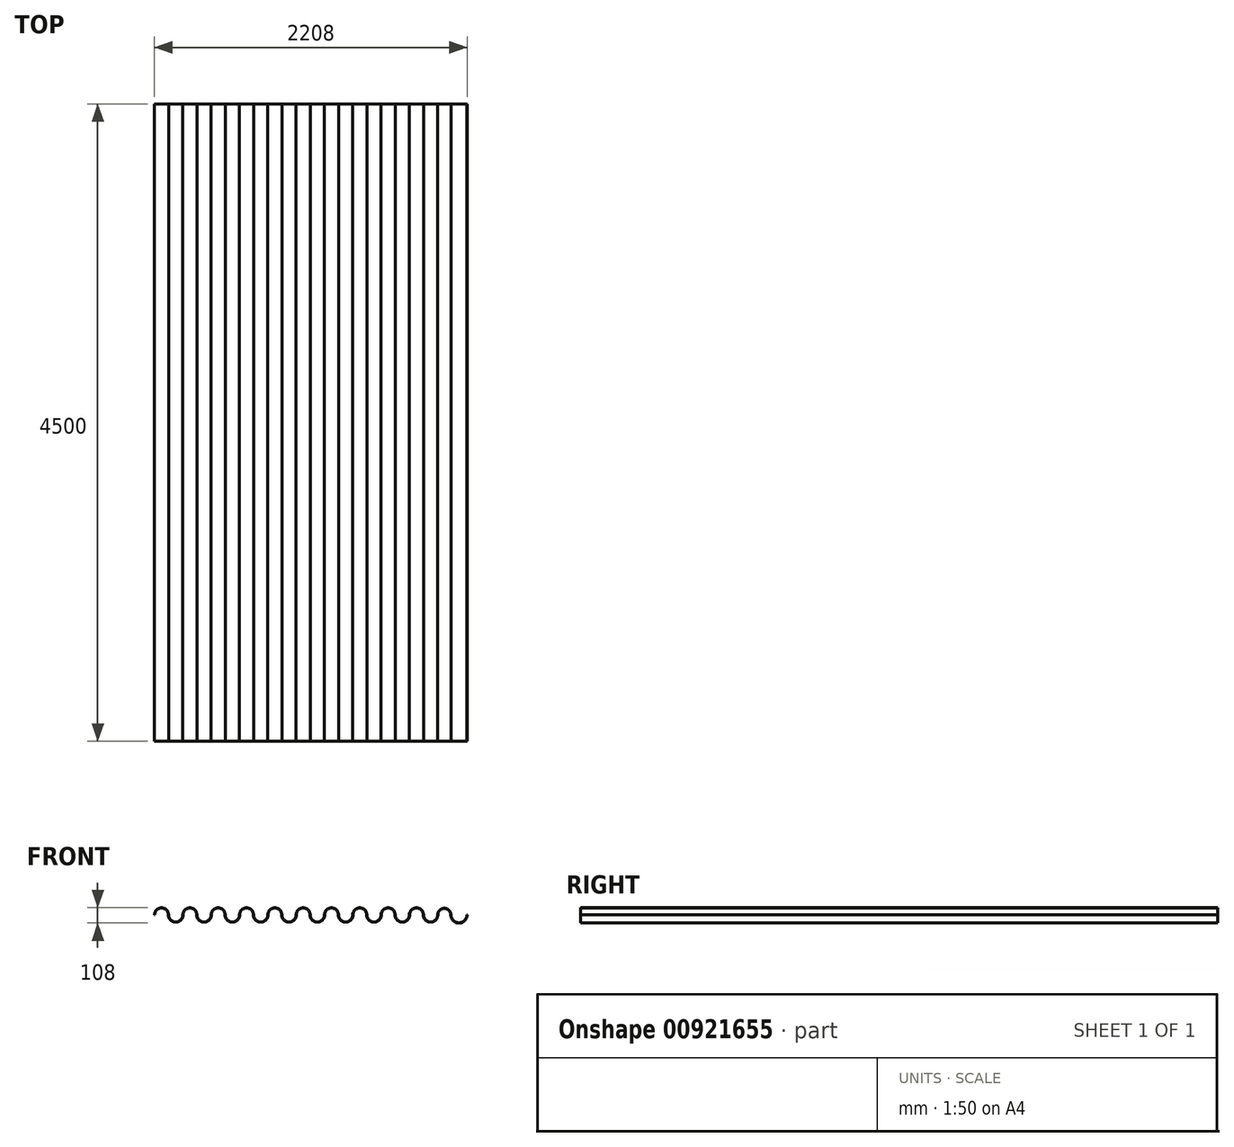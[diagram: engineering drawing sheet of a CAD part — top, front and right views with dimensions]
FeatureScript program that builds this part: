
annotation { "Feature Type Name" : "Feature", "Feature Type Description" : "" }
export const myFeature = defineFeature(function(context is Context, id is Id, definition is map)
    precondition{}
    {
        {
            var Q0;
            Q0=qCreatedBy(makeId("Front.planeOp"),FACE);
            var sketch = newSketch(context, id + "F0", { "sketchPlane" : qUnion([Q0])});
            skArc(sketch, "E0", {"start": v(50, 0) * mm, "mid": v(0, 50) * mm, "end": v(-50, 0) * mm});
            skArc(sketch, "E1", {"start": v(50, 0) * mm, "mid": v(100, -50) * mm, "end": v(150, 0) * mm});
            skArc(sketch, "E2", {"start": v(150, 0) * mm, "mid": v(200, 50) * mm, "end": v(250, 0) * mm});
            skArc(sketch, "E3", {"start": v(250, 0) * mm, "mid": v(300, -50) * mm, "end": v(350, 0) * mm});
            skArc(sketch, "E4", {"start": v(350, 0) * mm, "mid": v(400, 50) * mm, "end": v(450, 0) * mm});
            skArc(sketch, "E5", {"start": v(450, 0) * mm, "mid": v(500, -50) * mm, "end": v(550, 0) * mm});
            skArc(sketch, "E6", {"start": v(550, 0) * mm, "mid": v(600, 50) * mm, "end": v(650, 0) * mm});
            skArc(sketch, "E7", {"start": v(650, 0) * mm, "mid": v(700, -50) * mm, "end": v(750, 0) * mm});
            skArc(sketch, "E8", {"start": v(750, 0) * mm, "mid": v(800, 50) * mm, "end": v(850, 0) * mm});
            skArc(sketch, "E9", {"start": v(850, 0) * mm, "mid": v(900, -50) * mm, "end": v(950, 0) * mm});
            skArc(sketch, "E10", {"start": v(950, 0) * mm, "mid": v(1000, 50) * mm, "end": v(1050, 0) * mm});
            skArc(sketch, "E11", {"start": v(1050, 0) * mm, "mid": v(1100, -50) * mm, "end": v(1150, 0) * mm});
            skArc(sketch, "E12", {"start": v(1150, 0) * mm, "mid": v(1200, 50) * mm, "end": v(1250, 0) * mm});
            skArc(sketch, "E13", {"start": v(1250, 0) * mm, "mid": v(1300, -50) * mm, "end": v(1350, 0) * mm});
            skArc(sketch, "E14", {"start": v(1350, 0) * mm, "mid": v(1400, 50) * mm, "end": v(1450, 0) * mm});
            skArc(sketch, "E15", {"start": v(1450, 0) * mm, "mid": v(1500, -50) * mm, "end": v(1550, 0) * mm});
            skArc(sketch, "E16", {"start": v(1550, 0) * mm, "mid": v(1600, 50) * mm, "end": v(1650, 0) * mm});
            skArc(sketch, "E17", {"start": v(1650, 0) * mm, "mid": v(1700, -50) * mm, "end": v(1750, 0) * mm});
            skArc(sketch, "E18", {"start": v(1750, 0) * mm, "mid": v(1800, 50) * mm, "end": v(1850, 0) * mm});
            skArc(sketch, "E19", {"start": v(1850, 0) * mm, "mid": v(1900, -50) * mm, "end": v(1950, 0) * mm});
            skArc(sketch, "E20", {"start": v(1950, 0) * mm, "mid": v(1997, 47) * mm, "end": v(2044, 0) * mm});
            skArc(sketch, "E21", {"start": v(2044, 0) * mm, "mid": v(2100, -56) * mm, "end": v(2156, 0) * mm});
            skArc(sketch, "E22.0", {"start": v(2042, 0) * mm, "mid": v(2100, -58) * mm, "end": v(2158, 0) * mm});
            skArc(sketch, "E22.1", {"start": v(1952, 0) * mm, "mid": v(1997, 45) * mm, "end": v(2042, 0) * mm});
            skArc(sketch, "E22.2", {"start": v(1848, 0) * mm, "mid": v(1900, -52) * mm, "end": v(1952, 0) * mm});
            skArc(sketch, "E22.3", {"start": v(1752, 0) * mm, "mid": v(1800, 48) * mm, "end": v(1848, 0) * mm});
            skArc(sketch, "E22.4", {"start": v(1648, 0) * mm, "mid": v(1700, -52) * mm, "end": v(1752, 0) * mm});
            skArc(sketch, "E22.5", {"start": v(1552, 0) * mm, "mid": v(1600, 48) * mm, "end": v(1648, 0) * mm});
            skArc(sketch, "E22.6", {"start": v(1448, 0) * mm, "mid": v(1500, -52) * mm, "end": v(1552, 0) * mm});
            skArc(sketch, "E22.7", {"start": v(1352, 0) * mm, "mid": v(1400, 48) * mm, "end": v(1448, 0) * mm});
            skArc(sketch, "E22.8", {"start": v(1248, 0) * mm, "mid": v(1300, -52) * mm, "end": v(1352, 0) * mm});
            skArc(sketch, "E22.9", {"start": v(1152, 0) * mm, "mid": v(1200, 48) * mm, "end": v(1248, 0) * mm});
            skArc(sketch, "E22.10", {"start": v(1048, 0) * mm, "mid": v(1100, -52) * mm, "end": v(1152, 0) * mm});
            skArc(sketch, "E22.11", {"start": v(952, 0) * mm, "mid": v(1000, 48) * mm, "end": v(1048, 0) * mm});
            skArc(sketch, "E22.12", {"start": v(248, 0) * mm, "mid": v(300, -52) * mm, "end": v(352, 0) * mm});
            skArc(sketch, "E22.13", {"start": v(152, 0) * mm, "mid": v(200, 48) * mm, "end": v(248, 0) * mm});
            skArc(sketch, "E22.14", {"start": v(48, 0) * mm, "mid": v(100, -52) * mm, "end": v(152, 0) * mm});
            skArc(sketch, "E22.15", {"start": v(48, 0) * mm, "mid": v(0, 48) * mm, "end": v(-48, 0) * mm});
            skArc(sketch, "E22.16", {"start": v(352, 0) * mm, "mid": v(400, 48) * mm, "end": v(448, 0) * mm});
            skArc(sketch, "E22.17", {"start": v(448, 0) * mm, "mid": v(500, -52) * mm, "end": v(552, 0) * mm});
            skArc(sketch, "E22.18", {"start": v(552, 0) * mm, "mid": v(600, 48) * mm, "end": v(648, 0) * mm});
            skArc(sketch, "E22.19", {"start": v(648, 0) * mm, "mid": v(700, -52) * mm, "end": v(752, 0) * mm});
            skArc(sketch, "E22.20", {"start": v(752, 0) * mm, "mid": v(800, 48) * mm, "end": v(848, 0) * mm});
            skArc(sketch, "E22.21", {"start": v(848, 0) * mm, "mid": v(900, -52) * mm, "end": v(952, 0) * mm});
            skLineSegment(sketch, "E23", {"start": v(2156, 0) * mm, "end": v(2158, 0) * mm});
            skLineSegment(sketch, "E24", {"start": v(-50, 0) * mm, "end": v(-48, 0) * mm});
            skSolve(sketch);
        }
        {
            var Q0;
            Q0 = qSketchRegion(id + "F0", true);
            extrude(context, id + "F1", {"entities" : qUnion([Q0]), "depth" : 4500 * mm, "offsetDistance" : 25 * mm});
        }
    });
